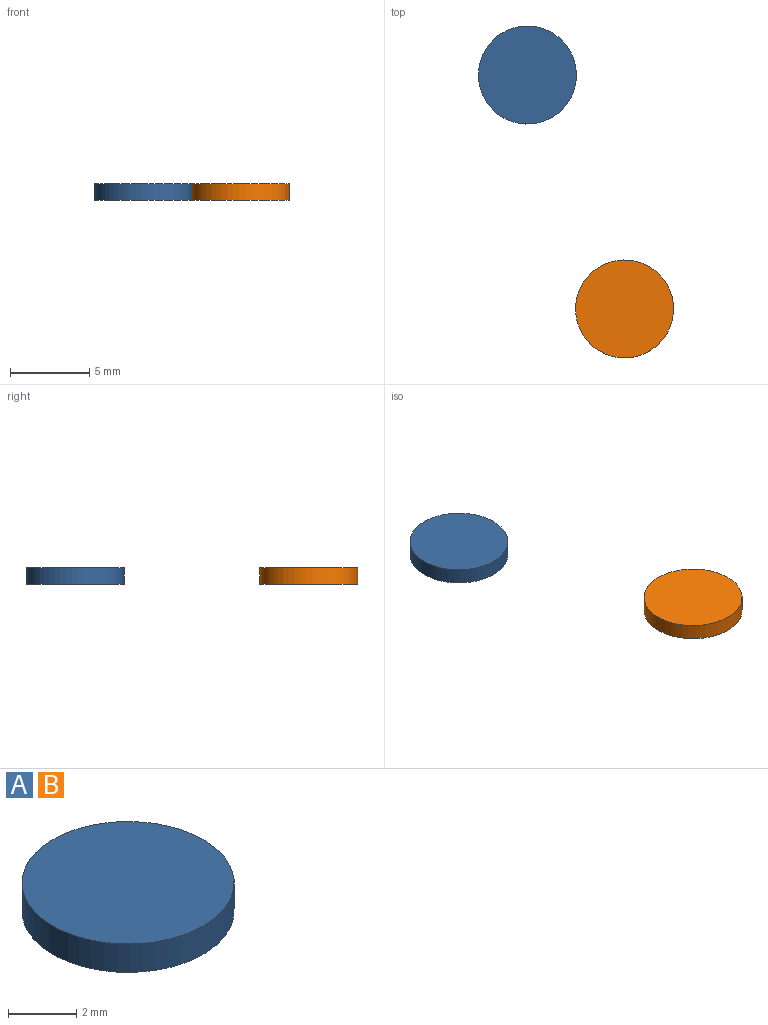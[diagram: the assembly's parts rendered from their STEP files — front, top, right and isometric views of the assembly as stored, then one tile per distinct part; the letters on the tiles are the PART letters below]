
ASSEMBLY  parts=2 mates=1
PART A: 3 faces, bbox 6.2x6.2x1 mm
  f0: cylinder r=3.1mm len=6.2mm, axis (0,0,-1), area 19.8mm2, adj f1,f2
  f1: plane 6.2x6.2mm, normal (0,0,1), area 30.2mm2, adj f0
  f2: plane 6.2x6.2mm, normal (0,0,-1), area 30.2mm2, adj f0
PART B: same geometry as A
PLACE A t=(-23.66,-13.6,0.8)mm fixed
PLACE B t=(-17.51,-28.4,0.8)mm
MATE planar A.f0 <-> B.f0  axis (0,0,1) through (-23.66,-13.6,1.81)mm
